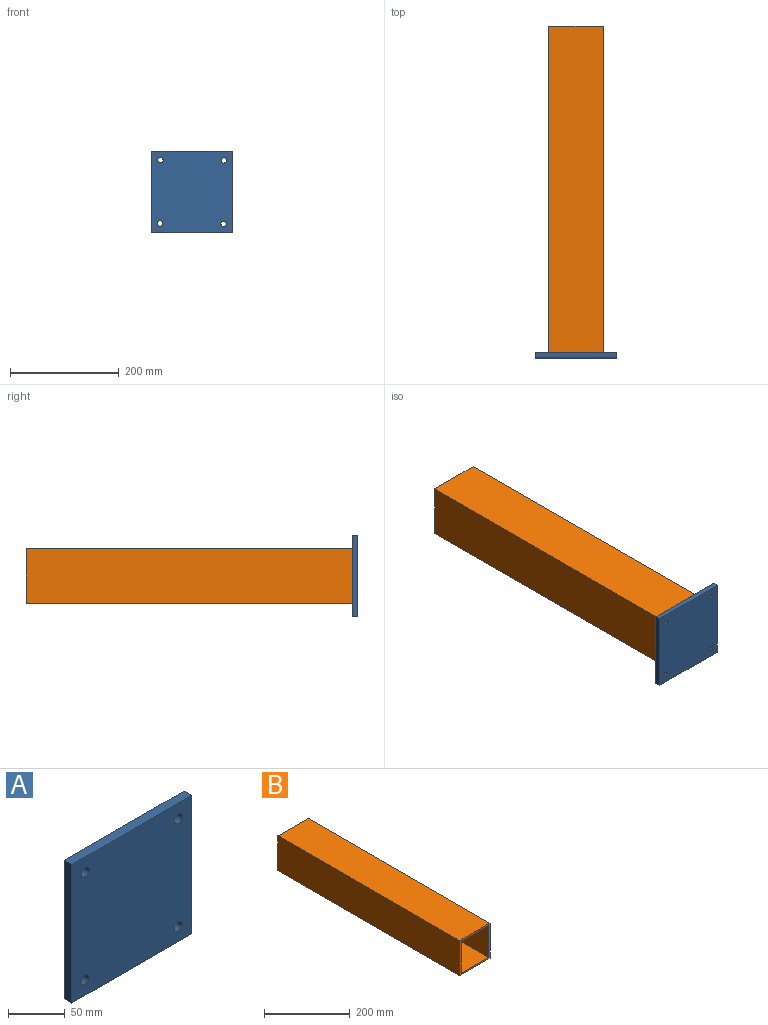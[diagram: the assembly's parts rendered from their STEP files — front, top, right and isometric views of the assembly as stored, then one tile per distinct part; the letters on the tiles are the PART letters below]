
ASSEMBLY  parts=2 mates=1
PART A: 10 faces, bbox 150x9.5x150 mm
  f0: plane 150x9.53mm, normal (1,0,0), area 1428.7mm2, adj f1,f3,f4,f5
  f1: plane 150x9.53mm, normal (0,0,1), area 1428.7mm2, adj f0,f2,f4,f5
  f2: plane 150x9.53mm, normal (-1,0,0), area 1428.7mm2, adj f1,f3,f4,f5
  f3: plane 150x9.53mm, normal (0,0,-1), area 1428.7mm2, adj f0,f2,f4,f5
  f4: plane 150x150mm, normal (0,-1,0), area 22180.6mm2, adj f0,f1,f2,f3,f6,f7,f8,f9
  f5: plane 150x150mm, normal (0,1,0), area 22180.6mm2, adj f0,f1,f2,f3,f6,f7,f8,f9
  f6: cylinder r=5.04mm len=10.08mm, axis (0,-1,0), area 301.7mm2, adj f4,f5
  f7: cylinder r=5.04mm len=10.08mm, axis (0,-1,0), area 301.7mm2, adj f4,f5
  f8: cylinder r=5.04mm len=10.08mm, axis (0,-1,0), area 301.7mm2, adj f4,f5
  f9: cylinder r=5.04mm len=10.08mm, axis (0,-1,0), area 301.7mm2, adj f4,f5
PART B: 10 faces, bbox 100x600x100 mm
  f0: plane 600x90.48mm, normal (0,0,-1), area 54285.6mm2, adj f1,f7,f8,f9
  f1: plane 600x90.48mm, normal (-1,0,0), area 54285.6mm2, adj f0,f2,f8,f9
  f2: plane 600x90.48mm, normal (0,0,1), area 54285.6mm2, adj f1,f7,f8,f9
  f3: plane 600x100mm, normal (1,0,0), area 60000mm2, adj f4,f6,f8,f9
  f4: plane 600x100mm, normal (0,0,1), area 60000mm2, adj f3,f5,f8,f9
  f5: plane 600x100mm, normal (-1,0,0), area 60000mm2, adj f4,f6,f8,f9
  f6: plane 600x100mm, normal (0,0,-1), area 60000mm2, adj f3,f5,f8,f9
  f7: plane 600x90.48mm, normal (1,0,0), area 54285.6mm2, adj f0,f2,f8,f9
  f8: plane 100x100mm, normal (0,-1,0), area 1814.1mm2, adj f0,f1,f2,f3,f4,f5,f6,f7
  f9: plane 100x100mm, normal (0,1,0), area 1814.1mm2, adj f0,f1,f2,f3,f4,f5,f6,f7
PLACE A t=(-35.23,-500.08,-76.15)mm
PLACE B t=(-35.23,99.92,-76.15)mm
MATE planar B.f8 <-> A.f5  axis (0,-1,0) through (-35.23,-500.08,-76.15)mm
